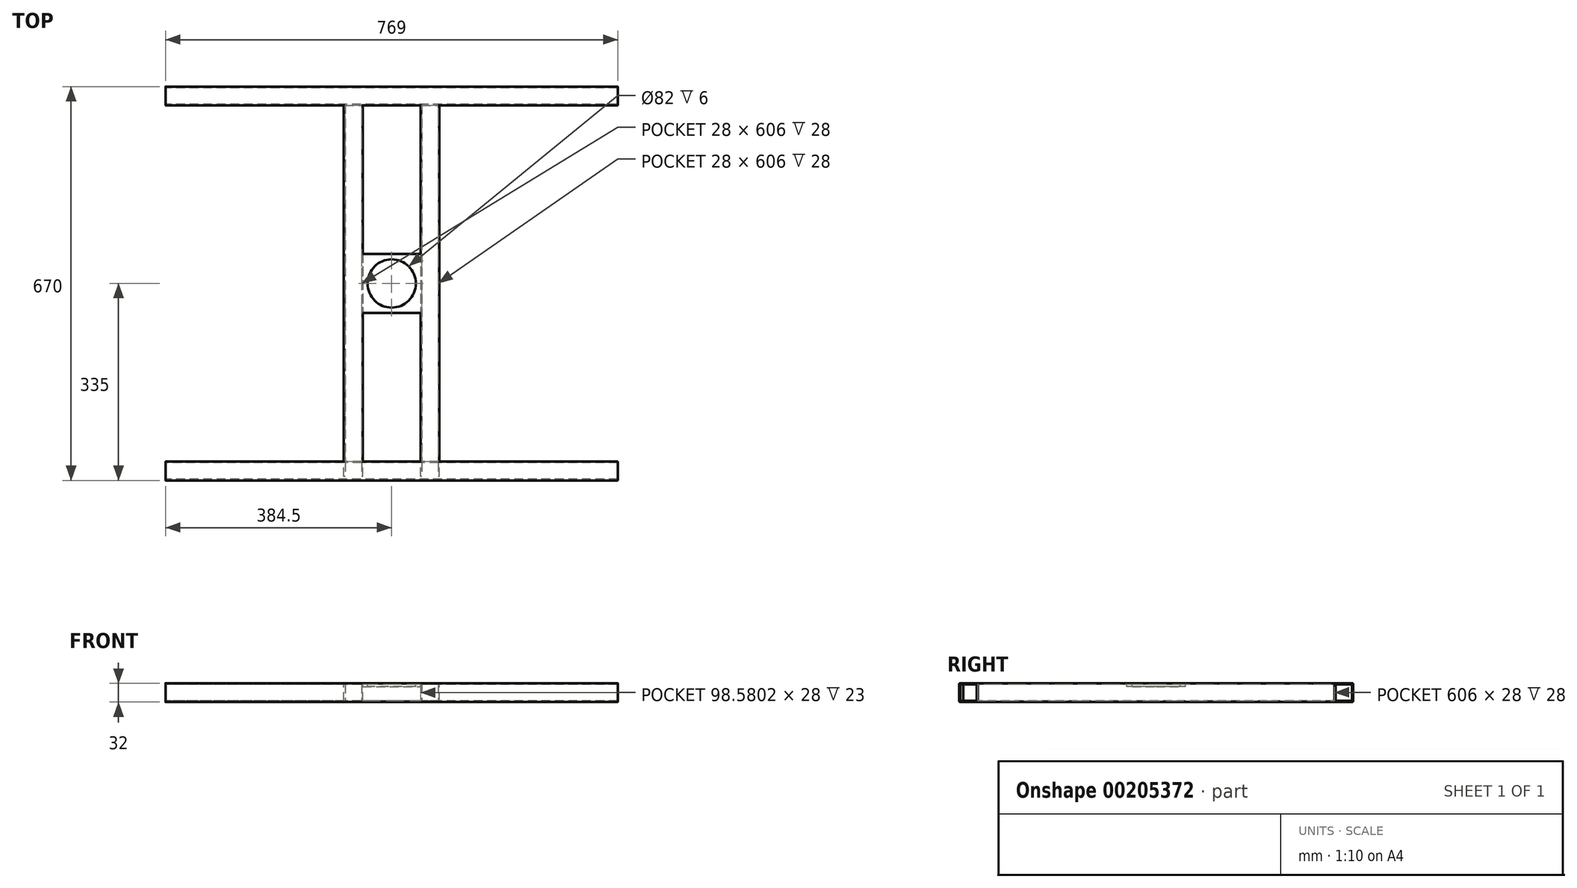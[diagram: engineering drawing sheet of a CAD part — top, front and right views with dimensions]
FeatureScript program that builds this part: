
annotation { "Feature Type Name" : "Feature", "Feature Type Description" : "" }
export const myFeature = defineFeature(function(context is Context, id is Id, definition is map)
    precondition{}
    {
        {
            var Q0;
            Q0=qCreatedBy(makeId("Right.planeOp"),FACE);
            var sketch = newSketch(context, id + "F0", { "sketchPlane" : qUnion([Q0])});
            skLineSegment(sketch, "E0.bottom", {"start": v(-333, -16) * mm, "end": v(-305, -16) * mm});
            skLineSegment(sketch, "E0.top", {"start": v(-333, 16) * mm, "end": v(-305, 16) * mm});
            skLineSegment(sketch, "E0.left", {"start": v(-335, -14) * mm, "end": v(-335, 14) * mm});
            skLineSegment(sketch, "E0.right", {"start": v(-303, -14) * mm, "end": v(-303, 14) * mm});
            skPoint(sketch, "E0.middle", {"position": v(-319, 0) * mm});
            skLineSegment(sketch, "E1.bottom", {"start": v(-333, 14) * mm, "end": v(-305, 14) * mm});
            skLineSegment(sketch, "E1.top", {"start": v(-333, -14) * mm, "end": v(-305, -14) * mm});
            skLineSegment(sketch, "E1.left", {"start": v(-333, 14) * mm, "end": v(-333, -14) * mm});
            skLineSegment(sketch, "E1.right", {"start": v(-305, 14) * mm, "end": v(-305, -14) * mm});
            skPoint(sketch, "E2.visualSharp", {"position": v(-335, 16) * mm});
            skArc(sketch, "E2.filletArc", {"start": v(-333, 16) * mm, "mid": v(-334.41, 15.41) * mm, "end": v(-335, 14) * mm});
            skPoint(sketch, "E3.visualSharp", {"position": v(-335, -16) * mm});
            skArc(sketch, "E3.filletArc", {"start": v(-335, -14) * mm, "mid": v(-334.41, -15.41) * mm, "end": v(-333, -16) * mm});
            skPoint(sketch, "E4.visualSharp", {"position": v(-303, -16) * mm});
            skArc(sketch, "E4.filletArc", {"start": v(-305, -16) * mm, "mid": v(-303.59, -15.41) * mm, "end": v(-303, -14) * mm});
            skPoint(sketch, "E5.visualSharp", {"position": v(-303, 16) * mm});
            skArc(sketch, "E5.filletArc", {"start": v(-303, 14) * mm, "mid": v(-303.59, 15.41) * mm, "end": v(-305, 16) * mm});
            skLineSegment(sketch, "E6", {"start": v(-319, 0) * mm, "end": v(0, 0) * mm, "construction": true});
            skArc(sketch, "E7.MirrorCS", {"start": v(333, 16) * mm, "mid": v(334.41, 15.41) * mm, "end": v(335, 14) * mm});
            skArc(sketch, "E8.MirrorCS", {"start": v(335, -14) * mm, "mid": v(334.41, -15.41) * mm, "end": v(333, -16) * mm});
            skArc(sketch, "E9.MirrorCS", {"start": v(303, 14) * mm, "mid": v(303.59, 15.41) * mm, "end": v(305, 16) * mm});
            skArc(sketch, "E10.MirrorCS", {"start": v(305, -16) * mm, "mid": v(303.59, -15.41) * mm, "end": v(303, -14) * mm});
            skPoint(sketch, "E11.MirrorP", {"position": v(319, 0) * mm});
            skLineSegment(sketch, "E12.MirrorCS", {"start": v(305, 14) * mm, "end": v(305, -14) * mm});
            skPoint(sketch, "E13.MirrorP", {"position": v(335, -16) * mm});
            skLineSegment(sketch, "E14.MirrorCS", {"start": v(333, 14) * mm, "end": v(333, -14) * mm});
            skLineSegment(sketch, "E15.MirrorCS", {"start": v(319, 0) * mm, "end": v(0, 0) * mm, "construction": true});
            skPoint(sketch, "E16.MirrorP", {"position": v(335, 16) * mm});
            skPoint(sketch, "E17.MirrorP", {"position": v(303, -16) * mm});
            skLineSegment(sketch, "E18.MirrorCS", {"start": v(333, -14) * mm, "end": v(305, -14) * mm});
            skLineSegment(sketch, "E19.MirrorCS", {"start": v(333, 14) * mm, "end": v(305, 14) * mm});
            skPoint(sketch, "E20.MirrorP", {"position": v(303, 16) * mm});
            skLineSegment(sketch, "E21.MirrorCS", {"start": v(303, -14) * mm, "end": v(303, 14) * mm});
            skLineSegment(sketch, "E22.MirrorCS", {"start": v(335, -14) * mm, "end": v(335, 14) * mm});
            skLineSegment(sketch, "E23.MirrorCS", {"start": v(333, 16) * mm, "end": v(305, 16) * mm});
            skLineSegment(sketch, "E24.MirrorCS", {"start": v(333, -16) * mm, "end": v(305, -16) * mm});
            skSolve(sketch);
        }
        {
            var Q0;
            Q0=qSketchRegion(id+"F0",true);
            extrude(context, id + "F1", {"entities" : qUnion([Q0]), "endBound" : BoundingType.SYMMETRIC, "depth" : 769 * mm});
        }
        {
            var Q0;
            Q0=makeQuery(id+"F1.opExtrude","SWEPT_FACE",FACE,{"disambiguationData":[OSD([sQuery(id+"F0.wireOp",EDGE,"E0.right")])]});
            var sketch = newSketch(context, id + "F2", { "sketchPlane" : qUnion([Q0])});
            skLineSegment(sketch, "E25", {"start": v(0, 14) * mm, "end": v(0, -14) * mm, "construction": true});
            skLineSegment(sketch, "E26", {"start": v(0, -14) * mm, "end": v(0, -6.92) * mm});
            skLineSegment(sketch, "E27", {"start": v(0, 0) * mm, "end": v(-65.3, 0) * mm, "construction": true});
            skPoint(sketch, "E27.endSnap0", {"position": v(0, 0) * mm});
            skLineSegment(sketch, "E28.bottom", {"start": v(-81.3, -16) * mm, "end": v(-49.3, -16) * mm});
            skLineSegment(sketch, "E28.top", {"start": v(-81.3, 16) * mm, "end": v(-49.3, 16) * mm});
            skLineSegment(sketch, "E28.left", {"start": v(-81.3, -16) * mm, "end": v(-81.3, 16) * mm});
            skLineSegment(sketch, "E28.right", {"start": v(-49.3, -16) * mm, "end": v(-49.3, 16) * mm});
            skPoint(sketch, "E28.middle", {"position": v(-65.3, 0) * mm});
            skLineSegment(sketch, "E29.0", {"start": v(-79.3, -14) * mm, "end": v(-79.3, 14) * mm});
            skLineSegment(sketch, "E29.1", {"start": v(-79.3, -14) * mm, "end": v(-51.3, -14) * mm});
            skLineSegment(sketch, "E29.2", {"start": v(-51.3, -14) * mm, "end": v(-51.3, 14) * mm});
            skLineSegment(sketch, "E29.3", {"start": v(-79.3, 14) * mm, "end": v(-51.3, 14) * mm});
            skLineSegment(sketch, "E30.MirrorCS", {"start": v(81.3, -16) * mm, "end": v(81.3, 16) * mm});
            skLineSegment(sketch, "E31.MirrorCS", {"start": v(81.3, 16) * mm, "end": v(49.3, 16) * mm});
            skLineSegment(sketch, "E32.MirrorCS", {"start": v(49.3, -16) * mm, "end": v(49.3, 16) * mm});
            skLineSegment(sketch, "E33.MirrorCS", {"start": v(81.3, -16) * mm, "end": v(49.3, -16) * mm});
            skLineSegment(sketch, "E34.MirrorCS", {"start": v(79.3, -14) * mm, "end": v(51.3, -14) * mm});
            skLineSegment(sketch, "E35.MirrorCS", {"start": v(79.3, -14) * mm, "end": v(79.3, 14) * mm});
            skLineSegment(sketch, "E36.MirrorCS", {"start": v(79.3, 14) * mm, "end": v(51.3, 14) * mm});
            skLineSegment(sketch, "E37.MirrorCS", {"start": v(51.3, -14) * mm, "end": v(51.3, 14) * mm});
            skLineSegment(sketch, "E38.bottom", {"start": v(51.15, 62.93) * mm, "end": v(-51.15, 62.93) * mm, "construction": true});
            skLineSegment(sketch, "E38.top", {"start": v(51.15, -62.93) * mm, "end": v(-51.15, -62.93) * mm, "construction": true});
            skLineSegment(sketch, "E38.left", {"start": v(51.15, 62.93) * mm, "end": v(51.15, -62.93) * mm, "construction": true});
            skLineSegment(sketch, "E38.right", {"start": v(-51.15, 62.93) * mm, "end": v(-51.15, -62.93) * mm, "construction": true});
            skSolve(sketch);
        }
        {
            var Q0;
            Q0=qSketchRegion(id+"F2",true);
            var Q1;
            Q1=qSketchRegion(id+"F2",true);
            extrude(context, id + "F3", {"entities" : qUnion([Q0, Q1]), "operationType" : NewBodyOperationType.ADD, "endBound" : BoundingType.UP_TO_NEXT, "depth" : 25 * mm, "hasSecondDirection" : true, "secondDirectionOppositeDirection" : true, "secondDirectionDepth" : 25 * mm});
        }
        {
            var Q0;
            Q0=makeQuery(id+"FsL87WSfcs1dLFI_2.boolean.opBoolean","MERGE",FACE,{"derivedFrom":[makeQuery(id+"F1.opExtrude","SWEPT_FACE",FACE,{"disambiguationData":[OSD([sQuery(id+"F0.wireOp",EDGE,"E23.MirrorCS")])]}),makeQuery(id+"FsL87WSfcs1dLFI_2.opExtrude","SWEPT_FACE",FACE,{"disambiguationData":[OSD([sQuery(id+"F2.wireOp",EDGE,"E28.top")])]}),makeQuery(id+"FsL87WSfcs1dLFI_2.opExtrude","SWEPT_FACE",FACE,{"disambiguationData":[OSD([sQuery(id+"F2.wireOp",EDGE,"E31.MirrorCS")])]})]});
            var sketch = newSketch(context, id + "F4", { "sketchPlane" : qUnion([Q0])});
            skPoint(sketch, "E39.middle", {"position": v(0, 0) * mm});
            skPoint(sketch, "E39.left.end.orphan", {"position": v(-50.7, 49.3) * mm});
            skPoint(sketch, "E39.bottom.start.orphan", {"position": v(-49.3, -50.7) * mm});
            skPoint(sketch, "E39.right.end.orphan", {"position": v(49.3, 50.7) * mm});
            skPoint(sketch, "E39.right.start.orphan", {"position": v(50.7, -49.3) * mm});
            skLineSegment(sketch, "E40.bottom", {"start": v(-50, -50) * mm, "end": v(50, -50) * mm});
            skLineSegment(sketch, "E40.top", {"start": v(-50, 50) * mm, "end": v(50, 50) * mm});
            skLineSegment(sketch, "E40.left", {"start": v(-50, -50) * mm, "end": v(-50, 50) * mm});
            skLineSegment(sketch, "E40.right", {"start": v(50, -50) * mm, "end": v(50, 50) * mm});
            skSolve(sketch);
        }
        {
            var Q0;
            {var subQ0=sQuery(id+"F4.wireOp",EDGE,"E40.bottom");var subQ1=makeQuery(id+"F3.opExtrude","SWEPT_EDGE",EDGE,{"disambiguationData":[OSD([sQuery(id+"F2.wireOp",EDGE,"E31.MirrorCS"),sQuery(id+"F2.wireOp",EDGE,"E32.MirrorCS")])]});var subQ2=makeQuery(id+"F4.imprint","INTERSECT",VERTEX,{"derivedFrom":[subQ1,subQ0]});Q0=makeQuery(id+"F4.imprint","IMPRINT",FACE,{"disambiguationData":[TD([[makeQuery(id+"F4.imprint","IMPRINT",EDGE,{"disambiguationData":[TD([[subQ2,-1.0]])],"derivedFrom":subQ0}),1.0]])]});}
            var Q1;
            {var subQ0=sQuery(id+"F4.wireOp",EDGE,"E40.bottom");var subQ1=makeQuery(id+"F3.opExtrude","SWEPT_EDGE",EDGE,{"disambiguationData":[OSD([sQuery(id+"F2.wireOp",EDGE,"E31.MirrorCS"),sQuery(id+"F2.wireOp",EDGE,"E32.MirrorCS")])]});var subQ2=makeQuery(id+"F4.imprint","INTERSECT",VERTEX,{"derivedFrom":[subQ1,subQ0]});Q1=makeQuery(id+"F4.imprint","IMPRINT",FACE,{"disambiguationData":[TD([[makeQuery(id+"F4.imprint","IMPRINT",EDGE,{"disambiguationData":[TD([[subQ2,-1.0]])],"derivedFrom":subQ0}),1.0]])]});}
            extrude(context, id + "F5", {"entities" : qUnion([Q0, Q1]), "operationType" : NewBodyOperationType.ADD, "oppositeDirection" : true, "depth" : 6 * mm});
        }
        {
            var Q0;
            Q0=makeQuery(id+"F5.boolean.opBoolean","MERGE",FACE,{"derivedFrom":[makeQuery(id+"FsL87WSfcs1dLFI_2.boolean.opBoolean","MERGE",FACE,{"derivedFrom":[makeQuery(id+"F1.opExtrude","SWEPT_FACE",FACE,{"disambiguationData":[OSD([sQuery(id+"F0.wireOp",EDGE,"E23.MirrorCS")])]}),makeQuery(id+"FsL87WSfcs1dLFI_2.opExtrude","SWEPT_FACE",FACE,{"disambiguationData":[OSD([sQuery(id+"F2.wireOp",EDGE,"E28.top")])]}),makeQuery(id+"FsL87WSfcs1dLFI_2.opExtrude","SWEPT_FACE",FACE,{"disambiguationData":[OSD([sQuery(id+"F2.wireOp",EDGE,"E31.MirrorCS")])]})]}),makeQuery(id+"F5.opExtrude","CAP_FACE",FACE,{"disambiguationData":[OSD([sQuery(id+"F4.wireOp",EDGE,"E40.bottom"),sQuery(id+"F4.wireOp",EDGE,"E40.top"),sQuery(id+"F4.wireOp",EDGE,"E40.left"),sQuery(id+"F4.wireOp",EDGE,"E40.right")])],"isStart":true})]});
            var sketch = newSketch(context, id + "F6", { "sketchPlane" : qUnion([Q0])});
            skCircle(sketch, "E41", {"center": v(0, 0) * mm, "radius": 41 * mm});
            skSolve(sketch);
        }
        {
            var Q0;
            Q0=qSketchRegion(id+"F6",true);
            extrude(context, id + "F7", {"entities" : qUnion([Q0]), "operationType" : NewBodyOperationType.REMOVE, "endBound" : BoundingType.THROUGH_ALL, "oppositeDirection" : true, "depth" : 25 * mm});
        }
    });
